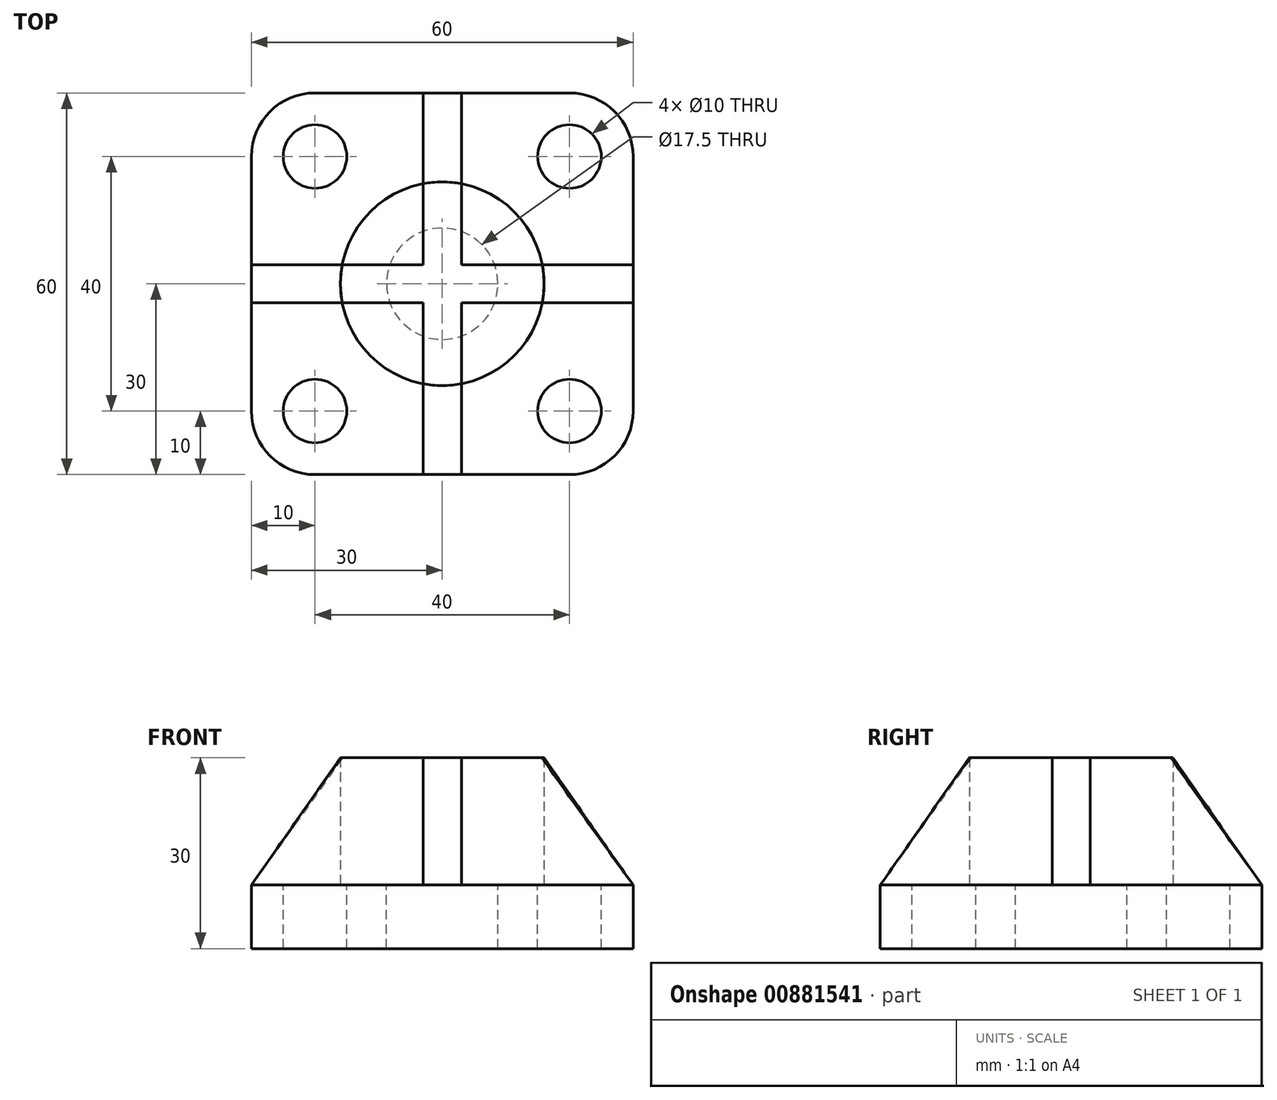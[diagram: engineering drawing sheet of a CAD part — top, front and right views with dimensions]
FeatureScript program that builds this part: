
annotation { "Feature Type Name" : "Feature", "Feature Type Description" : "" }
export const myFeature = defineFeature(function(context is Context, id is Id, definition is map)
    precondition{}
    {
        {
            var Q0;
            Q0=qCreatedBy(makeId("Top.planeOp"),FACE);
            var sketch = newSketch(context, id + "F0", { "sketchPlane" : qUnion([Q0])});
            skLineSegment(sketch, "E0.bottom", {"start": v(20, -30) * mm, "end": v(-20, -30) * mm});
            skLineSegment(sketch, "E0.top", {"start": v(20, 30) * mm, "end": v(-20, 30) * mm});
            skLineSegment(sketch, "E0.left", {"start": v(30, -20) * mm, "end": v(30, 20) * mm});
            skLineSegment(sketch, "E0.right", {"start": v(-30, -20) * mm, "end": v(-30, 20) * mm});
            skPoint(sketch, "E0.middle", {"position": v(0, 0) * mm});
            skLineSegment(sketch, "E1.bottom", {"start": v(20, -20) * mm, "end": v(-20, -20) * mm, "construction": true});
            skLineSegment(sketch, "E1.top", {"start": v(20, 20) * mm, "end": v(-20, 20) * mm, "construction": true});
            skLineSegment(sketch, "E1.left", {"start": v(20, -20) * mm, "end": v(20, 20) * mm, "construction": true});
            skLineSegment(sketch, "E1.right", {"start": v(-20, -20) * mm, "end": v(-20, 20) * mm, "construction": true});
            skCircle(sketch, "E2", {"center": v(0, 0) * mm, "radius": 16 * mm});
            skCircle(sketch, "E3", {"center": v(0, 0) * mm, "radius": 8 * mm});
            skLineSegment(sketch, "E4", {"start": v(-3, 30) * mm, "end": v(-3, -30) * mm, "construction": true});
            skLineSegment(sketch, "E5.MirrorCS", {"start": v(3, 30) * mm, "end": v(3, -30) * mm, "construction": true});
            skLineSegment(sketch, "E6", {"start": v(-30, 3) * mm, "end": v(30, 3) * mm, "construction": true});
            skLineSegment(sketch, "E7.MirrorCS", {"start": v(-30, -3) * mm, "end": v(30, -3) * mm, "construction": true});
            skPoint(sketch, "E8.visualSharp", {"position": v(-30, 30) * mm});
            skArc(sketch, "E8.filletArc", {"start": v(-20, 30) * mm, "mid": v(-27.07, 27.07) * mm, "end": v(-30, 20) * mm});
            skPoint(sketch, "E9.visualSharp", {"position": v(30, 30) * mm});
            skArc(sketch, "E9.filletArc", {"start": v(30, 20) * mm, "mid": v(27.07, 27.07) * mm, "end": v(20, 30) * mm});
            skPoint(sketch, "E10.visualSharp", {"position": v(30, -30) * mm});
            skArc(sketch, "E10.filletArc", {"start": v(20, -30) * mm, "mid": v(27.07, -27.07) * mm, "end": v(30, -20) * mm});
            skPoint(sketch, "E11.visualSharp", {"position": v(-30, -30) * mm});
            skArc(sketch, "E11.filletArc", {"start": v(-30, -20) * mm, "mid": v(-27.07, -27.07) * mm, "end": v(-20, -30) * mm});
            skSolve(sketch);
        }
        {
            var Q0;
            {var subQ1=sQuery(id+"F0.wireOp",EDGE,"E0.top");var subQ7=sQuery(id+"F0.wireOp",EDGE,"E0.right");var subQ8=makeQuery(id+"F0.imprint","INTERSECT",VERTEX,{"derivedFrom":[subQ1,subQ7]});Q0=makeQuery(id+"F0.imprint","IMPRINT",FACE,{"disambiguationData":[TD([[makeQuery(id+"F0.imprint","IMPRINT",EDGE,{"disambiguationData":[TD([[subQ8,1.0]])],"derivedFrom":subQ1}),1.0]])]});}
            var Q1;
            {var subQ0=sQuery(id+"F0.wireOp",EDGE,"E4");var subQ1=sQuery(id+"F0.wireOp",EDGE,"E2");var subQ2=makeQuery(id+"F0.imprint","INTERSECT",VERTEX,{"disambiguationData":[OD(0.0)],"derivedFrom":[subQ1,subQ0]});Q1=makeQuery(id+"F0.imprint","IMPRINT",FACE,{"disambiguationData":[TD([[makeQuery(id+"F0.imprint","IMPRINT",EDGE,{"disambiguationData":[TD([[subQ2,-1.0]])],"derivedFrom":subQ1}),1.0]])]});}
            var Q2;
            {var subQ0=sQuery(id+"F0.wireOp",EDGE,"E4");var subQ1=sQuery(id+"F0.wireOp",EDGE,"E3");var subQ2=makeQuery(id+"F0.imprint","INTERSECT",VERTEX,{"disambiguationData":[OD(0.0)],"derivedFrom":[subQ1,subQ0]});Q2=makeQuery(id+"F0.imprint","IMPRINT",FACE,{"disambiguationData":[TD([[makeQuery(id+"F0.imprint","IMPRINT",EDGE,{"disambiguationData":[TD([[subQ2,-1.0]])],"derivedFrom":subQ1}),1.0]])]});}
            var Q3;
            {var subQ0=sQuery(id+"F0.wireOp",EDGE,"E4");var subQ1=sQuery(id+"F0.wireOp",EDGE,"E0.top");var subQ2=makeQuery(id+"F0.imprint","INTERSECT",VERTEX,{"derivedFrom":[subQ1,subQ0]});Q3=makeQuery(id+"F0.imprint","IMPRINT",FACE,{"disambiguationData":[TD([[makeQuery(id+"F0.imprint","IMPRINT",EDGE,{"disambiguationData":[TD([[subQ2,1.0]])],"derivedFrom":subQ1}),1.0]])]});}
            var Q4;
            {var subQ0=sQuery(id+"F0.wireOp",EDGE,"E5.MirrorCS");var subQ1=sQuery(id+"F0.wireOp",EDGE,"E2");var subQ2=makeQuery(id+"F0.imprint","INTERSECT",VERTEX,{"disambiguationData":[OD(0.0)],"derivedFrom":[subQ1,subQ0]});Q4=makeQuery(id+"F0.imprint","IMPRINT",FACE,{"disambiguationData":[TD([[makeQuery(id+"F0.imprint","IMPRINT",EDGE,{"disambiguationData":[TD([[subQ2,-1.0]])],"derivedFrom":subQ1}),1.0]])]});}
            var Q5;
            {var subQ0=sQuery(id+"F0.wireOp",EDGE,"E5.MirrorCS");var subQ1=sQuery(id+"F0.wireOp",EDGE,"E3");var subQ2=makeQuery(id+"F0.imprint","INTERSECT",VERTEX,{"disambiguationData":[OD(0.0)],"derivedFrom":[subQ1,subQ0]});Q5=makeQuery(id+"F0.imprint","IMPRINT",FACE,{"disambiguationData":[TD([[makeQuery(id+"F0.imprint","IMPRINT",EDGE,{"disambiguationData":[TD([[subQ2,-1.0]])],"derivedFrom":subQ1}),1.0]])]});}
            var Q6;
            {var subQ1=sQuery(id+"F0.wireOp",EDGE,"E0.top");var subQ7=sQuery(id+"F0.wireOp",EDGE,"E0.left");var subQ8=makeQuery(id+"F0.imprint","INTERSECT",VERTEX,{"derivedFrom":[subQ1,subQ7]});Q6=makeQuery(id+"F0.imprint","IMPRINT",FACE,{"disambiguationData":[TD([[makeQuery(id+"F0.imprint","IMPRINT",EDGE,{"disambiguationData":[TD([[subQ8,-1.0]])],"derivedFrom":subQ1}),1.0]])]});}
            var Q7;
            {var subQ0=sQuery(id+"F0.wireOp",EDGE,"E5.MirrorCS");var subQ1=sQuery(id+"F0.wireOp",EDGE,"E2");var subQ2=makeQuery(id+"F0.imprint","INTERSECT",VERTEX,{"disambiguationData":[OD(0.0)],"derivedFrom":[subQ1,subQ0]});Q7=makeQuery(id+"F0.imprint","IMPRINT",FACE,{"disambiguationData":[TD([[makeQuery(id+"F0.imprint","IMPRINT",EDGE,{"disambiguationData":[TD([[subQ2,1.0]])],"derivedFrom":subQ1}),1.0]])]});}
            var Q8;
            {var subQ0=sQuery(id+"F0.wireOp",EDGE,"E5.MirrorCS");var subQ1=sQuery(id+"F0.wireOp",EDGE,"E3");var subQ2=makeQuery(id+"F0.imprint","INTERSECT",VERTEX,{"disambiguationData":[OD(0.0)],"derivedFrom":[subQ1,subQ0]});Q8=makeQuery(id+"F0.imprint","IMPRINT",FACE,{"disambiguationData":[TD([[makeQuery(id+"F0.imprint","IMPRINT",EDGE,{"disambiguationData":[TD([[subQ2,1.0]])],"derivedFrom":subQ1}),1.0]])]});}
            var Q9;
            {var subQ0=sQuery(id+"F0.wireOp",EDGE,"E6");var subQ1=sQuery(id+"F0.wireOp",EDGE,"E0.right");var subQ2=makeQuery(id+"F0.imprint","INTERSECT",VERTEX,{"derivedFrom":[subQ1,subQ0]});Q9=makeQuery(id+"F0.imprint","IMPRINT",FACE,{"disambiguationData":[TD([[makeQuery(id+"F0.imprint","IMPRINT",EDGE,{"disambiguationData":[TD([[subQ2,1.0]])],"derivedFrom":subQ1}),-1.0]])]});}
            var Q10;
            {var subQ0=sQuery(id+"F0.wireOp",EDGE,"E6");var subQ1=sQuery(id+"F0.wireOp",EDGE,"E2");var subQ2=makeQuery(id+"F0.imprint","INTERSECT",VERTEX,{"disambiguationData":[OD(1.0)],"derivedFrom":[subQ1,subQ0]});Q10=makeQuery(id+"F0.imprint","IMPRINT",FACE,{"disambiguationData":[TD([[makeQuery(id+"F0.imprint","IMPRINT",EDGE,{"disambiguationData":[TD([[subQ2,-1.0]])],"derivedFrom":subQ1}),1.0]])]});}
            var Q11;
            {var subQ0=sQuery(id+"F0.wireOp",EDGE,"E6");var subQ1=sQuery(id+"F0.wireOp",EDGE,"E3");var subQ2=makeQuery(id+"F0.imprint","INTERSECT",VERTEX,{"disambiguationData":[OD(1.0)],"derivedFrom":[subQ1,subQ0]});Q11=makeQuery(id+"F0.imprint","IMPRINT",FACE,{"disambiguationData":[TD([[makeQuery(id+"F0.imprint","IMPRINT",EDGE,{"disambiguationData":[TD([[subQ2,-1.0]])],"derivedFrom":subQ1}),1.0]])]});}
            var Q12;
            {var subQ0=sQuery(id+"F0.wireOp",EDGE,"E6");var subQ1=sQuery(id+"F0.wireOp",EDGE,"E4");var subQ2=makeQuery(id+"F0.imprint","INTERSECT",VERTEX,{"derivedFrom":[subQ1,subQ0]});Q12=makeQuery(id+"F0.imprint","IMPRINT",FACE,{"disambiguationData":[TD([[makeQuery(id+"F0.imprint","IMPRINT",EDGE,{"disambiguationData":[TD([[subQ2,-1.0]])],"derivedFrom":subQ1}),1.0]])]});}
            var Q13;
            {var subQ0=sQuery(id+"F0.wireOp",EDGE,"E6");var subQ1=sQuery(id+"F0.wireOp",EDGE,"E3");var subQ2=makeQuery(id+"F0.imprint","INTERSECT",VERTEX,{"disambiguationData":[OD(0.0)],"derivedFrom":[subQ1,subQ0]});Q13=makeQuery(id+"F0.imprint","IMPRINT",FACE,{"disambiguationData":[TD([[makeQuery(id+"F0.imprint","IMPRINT",EDGE,{"disambiguationData":[TD([[subQ2,1.0]])],"derivedFrom":subQ1}),1.0]])]});}
            var Q14;
            {var subQ0=sQuery(id+"F0.wireOp",EDGE,"E6");var subQ1=sQuery(id+"F0.wireOp",EDGE,"E2");var subQ2=makeQuery(id+"F0.imprint","INTERSECT",VERTEX,{"disambiguationData":[OD(0.0)],"derivedFrom":[subQ1,subQ0]});Q14=makeQuery(id+"F0.imprint","IMPRINT",FACE,{"disambiguationData":[TD([[makeQuery(id+"F0.imprint","IMPRINT",EDGE,{"disambiguationData":[TD([[subQ2,1.0]])],"derivedFrom":subQ1}),1.0]])]});}
            var Q15;
            {var subQ0=sQuery(id+"F0.wireOp",EDGE,"E6");var subQ1=sQuery(id+"F0.wireOp",EDGE,"E0.left");var subQ2=makeQuery(id+"F0.imprint","INTERSECT",VERTEX,{"derivedFrom":[subQ1,subQ0]});Q15=makeQuery(id+"F0.imprint","IMPRINT",FACE,{"disambiguationData":[TD([[makeQuery(id+"F0.imprint","IMPRINT",EDGE,{"disambiguationData":[TD([[subQ2,1.0]])],"derivedFrom":subQ1}),1.0]])]});}
            var Q16;
            {var subQ0=sQuery(id+"F0.wireOp",EDGE,"E7.MirrorCS");var subQ1=sQuery(id+"F0.wireOp",EDGE,"E3");var subQ2=makeQuery(id+"F0.imprint","INTERSECT",VERTEX,{"disambiguationData":[OD(0.0)],"derivedFrom":[subQ1,subQ0]});Q16=makeQuery(id+"F0.imprint","IMPRINT",FACE,{"disambiguationData":[TD([[makeQuery(id+"F0.imprint","IMPRINT",EDGE,{"disambiguationData":[TD([[subQ2,-1.0]])],"derivedFrom":subQ1}),1.0]])]});}
            var Q17;
            {var subQ0=sQuery(id+"F0.wireOp",EDGE,"E4");var subQ1=sQuery(id+"F0.wireOp",EDGE,"E3");var subQ2=makeQuery(id+"F0.imprint","INTERSECT",VERTEX,{"disambiguationData":[OD(1.0)],"derivedFrom":[subQ1,subQ0]});Q17=makeQuery(id+"F0.imprint","IMPRINT",FACE,{"disambiguationData":[TD([[makeQuery(id+"F0.imprint","IMPRINT",EDGE,{"disambiguationData":[TD([[subQ2,-1.0]])],"derivedFrom":subQ1}),1.0]])]});}
            var Q18;
            {var subQ0=sQuery(id+"F0.wireOp",EDGE,"E5.MirrorCS");var subQ1=sQuery(id+"F0.wireOp",EDGE,"E3");var subQ2=makeQuery(id+"F0.imprint","INTERSECT",VERTEX,{"disambiguationData":[OD(1.0)],"derivedFrom":[subQ1,subQ0]});Q18=makeQuery(id+"F0.imprint","IMPRINT",FACE,{"disambiguationData":[TD([[makeQuery(id+"F0.imprint","IMPRINT",EDGE,{"disambiguationData":[TD([[subQ2,-1.0]])],"derivedFrom":subQ1}),1.0]])]});}
            var Q19;
            {var subQ0=sQuery(id+"F0.wireOp",EDGE,"E7.MirrorCS");var subQ1=sQuery(id+"F0.wireOp",EDGE,"E2");var subQ2=makeQuery(id+"F0.imprint","INTERSECT",VERTEX,{"disambiguationData":[OD(0.0)],"derivedFrom":[subQ1,subQ0]});Q19=makeQuery(id+"F0.imprint","IMPRINT",FACE,{"disambiguationData":[TD([[makeQuery(id+"F0.imprint","IMPRINT",EDGE,{"disambiguationData":[TD([[subQ2,-1.0]])],"derivedFrom":subQ1}),1.0]])]});}
            var Q20;
            {var subQ0=sQuery(id+"F0.wireOp",EDGE,"E4");var subQ1=sQuery(id+"F0.wireOp",EDGE,"E2");var subQ2=makeQuery(id+"F0.imprint","INTERSECT",VERTEX,{"disambiguationData":[OD(1.0)],"derivedFrom":[subQ1,subQ0]});Q20=makeQuery(id+"F0.imprint","IMPRINT",FACE,{"disambiguationData":[TD([[makeQuery(id+"F0.imprint","IMPRINT",EDGE,{"disambiguationData":[TD([[subQ2,-1.0]])],"derivedFrom":subQ1}),1.0]])]});}
            var Q21;
            {var subQ0=sQuery(id+"F0.wireOp",EDGE,"E5.MirrorCS");var subQ1=sQuery(id+"F0.wireOp",EDGE,"E2");var subQ2=makeQuery(id+"F0.imprint","INTERSECT",VERTEX,{"disambiguationData":[OD(1.0)],"derivedFrom":[subQ1,subQ0]});Q21=makeQuery(id+"F0.imprint","IMPRINT",FACE,{"disambiguationData":[TD([[makeQuery(id+"F0.imprint","IMPRINT",EDGE,{"disambiguationData":[TD([[subQ2,-1.0]])],"derivedFrom":subQ1}),1.0]])]});}
            var Q22;
            {var subQ5=sQuery(id+"F0.wireOp",EDGE,"E0.right");var subQ7=sQuery(id+"F0.wireOp",EDGE,"E0.bottom");var subQ9=makeQuery(id+"F0.imprint","INTERSECT",VERTEX,{"derivedFrom":[subQ7,subQ5]});Q22=makeQuery(id+"F0.imprint","IMPRINT",FACE,{"disambiguationData":[TD([[makeQuery(id+"F0.imprint","IMPRINT",EDGE,{"disambiguationData":[TD([[subQ9,1.0]])],"derivedFrom":subQ7}),-1.0]])]});}
            var Q23;
            {var subQ0=sQuery(id+"F0.wireOp",EDGE,"E4");var subQ1=sQuery(id+"F0.wireOp",EDGE,"E0.bottom");var subQ2=makeQuery(id+"F0.imprint","INTERSECT",VERTEX,{"derivedFrom":[subQ1,subQ0]});Q23=makeQuery(id+"F0.imprint","IMPRINT",FACE,{"disambiguationData":[TD([[makeQuery(id+"F0.imprint","IMPRINT",EDGE,{"disambiguationData":[TD([[subQ2,1.0]])],"derivedFrom":subQ1}),-1.0]])]});}
            var Q24;
            {var subQ5=sQuery(id+"F0.wireOp",EDGE,"E0.bottom");var subQ7=sQuery(id+"F0.wireOp",EDGE,"E0.left");var subQ8=makeQuery(id+"F0.imprint","INTERSECT",VERTEX,{"derivedFrom":[subQ5,subQ7]});Q24=makeQuery(id+"F0.imprint","IMPRINT",FACE,{"disambiguationData":[TD([[makeQuery(id+"F0.imprint","IMPRINT",EDGE,{"disambiguationData":[TD([[subQ8,-1.0]])],"derivedFrom":subQ5}),-1.0]])]});}
            var Q25;
            {var subQ7=sQuery(id+"F0.wireOp",EDGE,"E8.filletArc");Q25=makeQuery(id+"F0.imprint","IMPRINT",FACE,{"disambiguationData":[TD([[makeQuery(id+"F0.imprint","IMPRINT",EDGE,{"derivedFrom":subQ7}),1.0]])]});}
            var Q26;
            {var subQ5=sQuery(id+"F0.wireOp",EDGE,"E9.filletArc");Q26=makeQuery(id+"F0.imprint","IMPRINT",FACE,{"disambiguationData":[TD([[makeQuery(id+"F0.imprint","IMPRINT",EDGE,{"derivedFrom":subQ5}),1.0]])]});}
            var Q27;
            {var subQ9=sQuery(id+"F0.wireOp",EDGE,"E11.filletArc");Q27=makeQuery(id+"F0.imprint","IMPRINT",FACE,{"disambiguationData":[TD([[makeQuery(id+"F0.imprint","IMPRINT",EDGE,{"derivedFrom":subQ9}),1.0]])]});}
            var Q28;
            {var subQ7=sQuery(id+"F0.wireOp",EDGE,"E10.filletArc");Q28=makeQuery(id+"F0.imprint","IMPRINT",FACE,{"disambiguationData":[TD([[makeQuery(id+"F0.imprint","IMPRINT",EDGE,{"derivedFrom":subQ7}),1.0]])]});}
            extrude(context, id + "F1", {"entities" : qUnion([Q0, Q1, Q2, Q3, Q4, Q5, Q6, Q7, Q8, Q9, Q10, Q11, Q12, Q13, Q14, Q15, Q16, Q17, Q18, Q19, Q20, Q21, Q22, Q23, Q24, Q25, Q26, Q27, Q28]), "oppositeDirection" : true, "depth" : 10 * mm, "offsetDistance" : 25 * mm});
        }
        {
            var Q0;
            Q0=makeQuery(id+"F0.imprint","IMPRINT",FACE,{"disambiguationData":[TD([[makeQuery(id+"F0.imprint","IMPRINT",EDGE,{"derivedFrom":sQuery(id+"F0.wireOp",EDGE,"E2")}),1.0]])]});
            var Q1;
            Q1=makeQuery(id+"F0.imprint","IMPRINT",FACE,{"disambiguationData":[TD([[makeQuery(id+"F0.imprint","IMPRINT",EDGE,{"derivedFrom":sQuery(id+"F0.wireOp",EDGE,"E3")}),1.0]])]});
            extrude(context, id + "F2", {"entities" : qUnion([Q0, Q1]), "depth" : 20 * mm, "offsetDistance" : 25 * mm});
        }
        {
            var Q0;
            Q0=qCreatedBy(makeId("Top.planeOp"),FACE);
            var sketch = newSketch(context, id + "F3", { "sketchPlane" : qUnion([Q0])});
            skLineSegment(sketch, "E12.0", {"start": v(20, 30) * mm, "end": v(-20, 30) * mm});
            skArc(sketch, "E12.1", {"start": v(-20, 30) * mm, "mid": v(-27.07, 27.07) * mm, "end": v(-30, 20) * mm});
            skLineSegment(sketch, "E12.2", {"start": v(-30, -20) * mm, "end": v(-30, 20) * mm});
            skLineSegment(sketch, "E12.3", {"start": v(20, -30) * mm, "end": v(-20, -30) * mm});
            skArc(sketch, "E12.4", {"start": v(-30, -20) * mm, "mid": v(-27.07, -27.07) * mm, "end": v(-20, -30) * mm});
            skArc(sketch, "E12.5", {"start": v(20, -30) * mm, "mid": v(27.07, -27.07) * mm, "end": v(30, -20) * mm});
            skLineSegment(sketch, "E12.6", {"start": v(30, -20) * mm, "end": v(30, 20) * mm});
            skArc(sketch, "E12.7", {"start": v(30, 20) * mm, "mid": v(27.07, 27.07) * mm, "end": v(20, 30) * mm});
            skSolve(sketch);
        }
        {
            var Q0;
            Q0 = qSketchRegion(id + "F3", true);
            var Q1;
            Q1=makeQuery(id+"F2.opExtrude","CAP_FACE",FACE,{"disambiguationData":[OSD([sQuery(id+"F0.wireOp",EDGE,"E2")])],"isStart":false});
            loft(context, id + "F4", {"sheetProfilesArray" : [{ "sheetProfileEntities" : qUnion([Q0]) }, { "sheetProfileEntities" : qUnion([Q1]) }]});
        }
        {
            var Q0;
            Q0=qCreatedBy(makeId("Top.planeOp"),FACE);
            var sketch = newSketch(context, id + "F5", { "sketchPlane" : qUnion([Q0])});
            skLineSegment(sketch, "E13.0", {"start": v(-3, 30) * mm, "end": v(-3, -30) * mm});
            skLineSegment(sketch, "E13.1", {"start": v(3, 30) * mm, "end": v(3, -30) * mm});
            skLineSegment(sketch, "E13.2", {"start": v(-30, 3) * mm, "end": v(30, 3) * mm});
            skLineSegment(sketch, "E13.3", {"start": v(-30, -3) * mm, "end": v(30, -3) * mm});
            skLineSegment(sketch, "E13.4", {"start": v(20, 30) * mm, "end": v(-20, 30) * mm});
            skLineSegment(sketch, "E13.5", {"start": v(-30, -20) * mm, "end": v(-30, 20) * mm});
            skLineSegment(sketch, "E13.6", {"start": v(30, -20) * mm, "end": v(30, 20) * mm});
            skLineSegment(sketch, "E13.7", {"start": v(20, -30) * mm, "end": v(-20, -30) * mm});
            skSolve(sketch);
        }
        {
            var Q0;
            {var subQ0=sQuery(id+"F5.wireOp",EDGE,"E13.2");var subQ1=sQuery(id+"F5.wireOp",EDGE,"E13.0");var subQ2=makeQuery(id+"F5.imprint","INTERSECT",VERTEX,{"derivedFrom":[subQ1,subQ0]});Q0=makeQuery(id+"F5.imprint","IMPRINT",FACE,{"disambiguationData":[TD([[makeQuery(id+"F5.imprint","IMPRINT",EDGE,{"disambiguationData":[TD([[subQ2,-1.0]])],"derivedFrom":subQ1}),-1.0]])]});}
            var Q1;
            {var subQ0=sQuery(id+"F5.wireOp",EDGE,"E13.4");var subQ1=sQuery(id+"F5.wireOp",EDGE,"E13.0");var subQ2=makeQuery(id+"F5.imprint","INTERSECT",VERTEX,{"derivedFrom":[subQ1,subQ0]});Q1=makeQuery(id+"F5.imprint","IMPRINT",FACE,{"disambiguationData":[TD([[makeQuery(id+"F5.imprint","IMPRINT",EDGE,{"disambiguationData":[TD([[subQ2,-1.0]])],"derivedFrom":subQ1}),1.0]])]});}
            var Q2;
            {var subQ0=sQuery(id+"F5.wireOp",EDGE,"E13.2");var subQ1=sQuery(id+"F5.wireOp",EDGE,"E13.1");var subQ2=makeQuery(id+"F5.imprint","INTERSECT",VERTEX,{"derivedFrom":[subQ1,subQ0]});Q2=makeQuery(id+"F5.imprint","IMPRINT",FACE,{"disambiguationData":[TD([[makeQuery(id+"F5.imprint","IMPRINT",EDGE,{"disambiguationData":[TD([[subQ2,-1.0]])],"derivedFrom":subQ1}),1.0]])]});}
            var Q3;
            {var subQ0=sQuery(id+"F5.wireOp",EDGE,"E13.7");var subQ1=sQuery(id+"F5.wireOp",EDGE,"E13.0");var subQ2=makeQuery(id+"F5.imprint","INTERSECT",VERTEX,{"derivedFrom":[subQ1,subQ0]});Q3=makeQuery(id+"F5.imprint","IMPRINT",FACE,{"disambiguationData":[TD([[makeQuery(id+"F5.imprint","IMPRINT",EDGE,{"disambiguationData":[TD([[subQ2,1.0]])],"derivedFrom":subQ1}),1.0]])]});}
            var Q4;
            {var subQ0=sQuery(id+"F5.wireOp",EDGE,"E13.2");var subQ1=sQuery(id+"F5.wireOp",EDGE,"E13.0");var subQ2=makeQuery(id+"F5.imprint","INTERSECT",VERTEX,{"derivedFrom":[subQ1,subQ0]});Q4=makeQuery(id+"F5.imprint","IMPRINT",FACE,{"disambiguationData":[TD([[makeQuery(id+"F5.imprint","IMPRINT",EDGE,{"disambiguationData":[TD([[subQ2,-1.0]])],"derivedFrom":subQ1}),1.0]])]});}
            extrude(context, id + "F6", {"entities" : qUnion([Q0, Q1, Q2, Q3, Q4]), "depth" : 25 * mm, "offsetDistance" : 25 * mm});
        }
        {
            var Q0;
            Q0=makeQuery(id+"F4.opLoft","SWEPT_BODY",BODY,{"disambiguationData":[OSD([sQuery(id+"F0.wireOp",EDGE,"E2"),makeQuery(id+"F3.imprint","IMPRINT",FACE,{"disambiguationData":[TD([[makeQuery(id+"F3.imprint","IMPRINT",EDGE,{"derivedFrom":sQuery(id+"F3.wireOp",EDGE,"E12.0")}),1.0]])]})])]});
            var Q1;
            Q1=makeQuery(id+"F6.opExtrude","SWEPT_BODY",BODY,{"disambiguationData":[OSD([sQuery(id+"F5.wireOp",EDGE,"E13.0"),sQuery(id+"F5.wireOp",EDGE,"E13.1"),sQuery(id+"F5.wireOp",EDGE,"E13.2"),sQuery(id+"F5.wireOp",EDGE,"E13.4")])]});
            booleanBodies(context, id + "F7", {"operationType" : BooleanOperationType.INTERSECTION, "tools" : qUnion([Q0, Q1])});
        }
        {
            var Q0;
            Q0=makeQuery(id+"F2.opExtrude","CAP_FACE",FACE,{"disambiguationData":[OSD([sQuery(id+"F0.wireOp",EDGE,"E2")])],"isStart":false});
            var sketch = newSketch(context, id + "F8", { "sketchPlane" : qUnion([Q0])});
            skPoint(sketch, "E14.0", {"position": v(0, 0) * mm});
            skSolve(sketch);
        }
        {
            var Q0;
            Q0=sQuery(id+"F8.wireOp",VERTEX,"E14.0");
            var Q1;
            Q1=makeQuery(id+"F1.opExtrude","SWEPT_BODY",BODY,{"disambiguationData":[OSD([sQuery(id+"F0.wireOp",EDGE,"E0.bottom"),sQuery(id+"F0.wireOp",EDGE,"E0.top"),sQuery(id+"F0.wireOp",EDGE,"E0.left"),sQuery(id+"F0.wireOp",EDGE,"E0.right")])]});
            hole(context, id + "F9", {"style" : HoleStyle.SIMPLE, "endStyle" : HoleEndStyle.THROUGH, "standardTappedOrClearance" : lookupTablePath({ "fit" : "Normal", "standard" : "ISO", "size" : "M16", "type" : "Clearance" }), "standardBlindInLast" : lookupTablePath({ "fit" : "Normal", "standard" : "ISO", "size" : "M16", "type" : "Clearance" }), "holeDiameter" : 17.5 * mm, "majorDiameter" : 5 * mm, "isTappedThrough" : true, "tappedDepth" : 12 * mm, "tapClearance" : 3, "startFromSketch" : true, "locations" : qUnion([Q0]), "scope" : qUnion([Q1])});
        }
        {
            var Q0;
            Q0=sQuery(id+"F0.wireOp",VERTEX,"E1.top.end");
            var Q1;
            Q1=sQuery(id+"F0.wireOp",VERTEX,"E1.top.start");
            var Q2;
            Q2=sQuery(id+"F0.wireOp",VERTEX,"E1.bottom.end");
            var Q3;
            Q3=sQuery(id+"F0.wireOp",VERTEX,"E1.bottom.start");
            var Q4;
            Q4=makeQuery(id+"F1.opExtrude","SWEPT_BODY",BODY,{"disambiguationData":[OSD([sQuery(id+"F0.wireOp",EDGE,"E0.bottom"),sQuery(id+"F0.wireOp",EDGE,"E0.top"),sQuery(id+"F0.wireOp",EDGE,"E0.left"),sQuery(id+"F0.wireOp",EDGE,"E0.right"),sQuery(id+"F0.wireOp",EDGE,"E3")])]});
            hole(context, id + "F10", {"style" : HoleStyle.SIMPLE, "endStyle" : HoleEndStyle.THROUGH, "holeDiameter" : 10 * mm, "majorDiameter" : 5 * mm, "isTappedThrough" : true, "tappedDepth" : 12 * mm, "tapClearance" : 3, "startFromSketch" : true, "locations" : qUnion([Q0, Q1, Q2, Q3]), "scope" : qUnion([Q4])});
        }
    });
